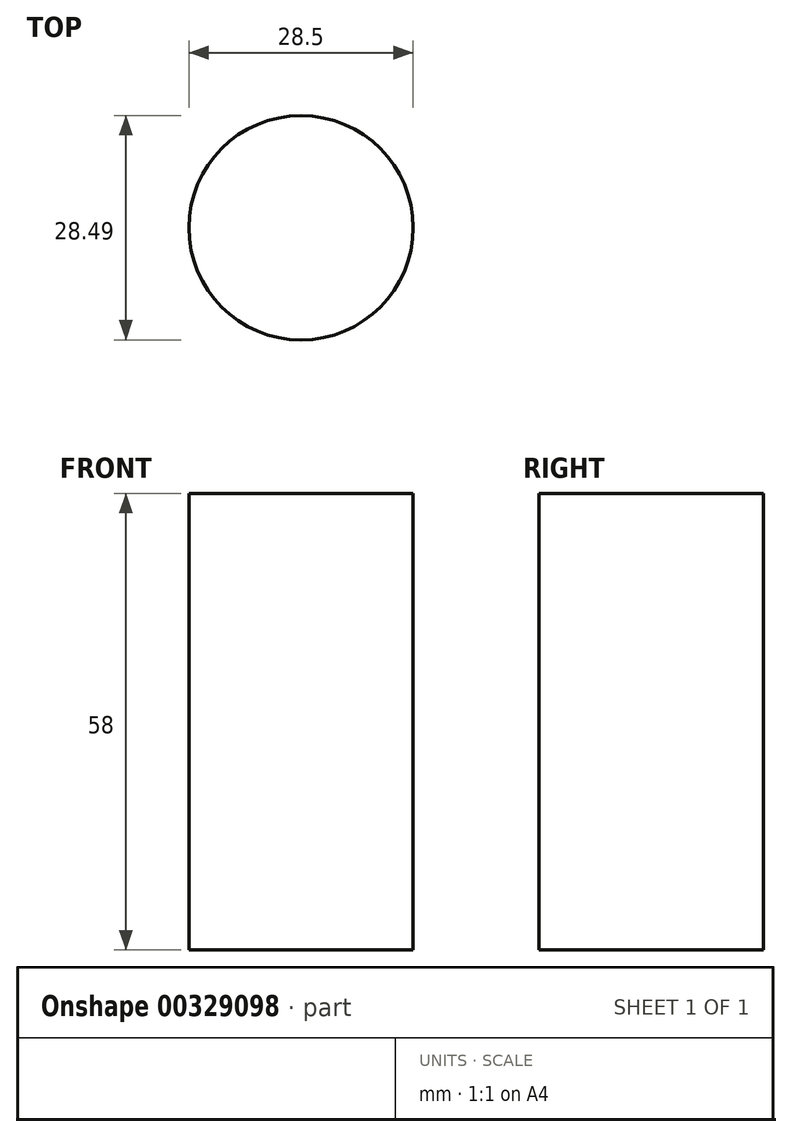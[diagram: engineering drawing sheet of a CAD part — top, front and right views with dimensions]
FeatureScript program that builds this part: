
annotation { "Feature Type Name" : "Feature", "Feature Type Description" : "" }
export const myFeature = defineFeature(function(context is Context, id is Id, definition is map)
    precondition{}
    {
        {
            var Q0;
            Q0=qCreatedBy(makeId("Top.planeOp"),FACE);
            var sketch = newSketch(context, id + "F0", { "sketchPlane" : qUnion([Q0])});
            skCircle(sketch, "E0", {"center": v(0, 2.77) * mm, "radius": 14.25 * mm});
            skSolve(sketch);
        }
        {
            var Q0;
            Q0=makeQuery(id+"F0.imprint","IMPRINT",FACE,{"disambiguationData":[TD([[makeQuery(id+"F0.imprint","IMPRINT",EDGE,{"derivedFrom":sQuery(id+"F0.wireOp",EDGE,"E0")}),1.0]])]});
            extrude(context, id + "F1", {"entities" : qUnion([Q0]), "depth" : 58 * mm});
        }
    });
